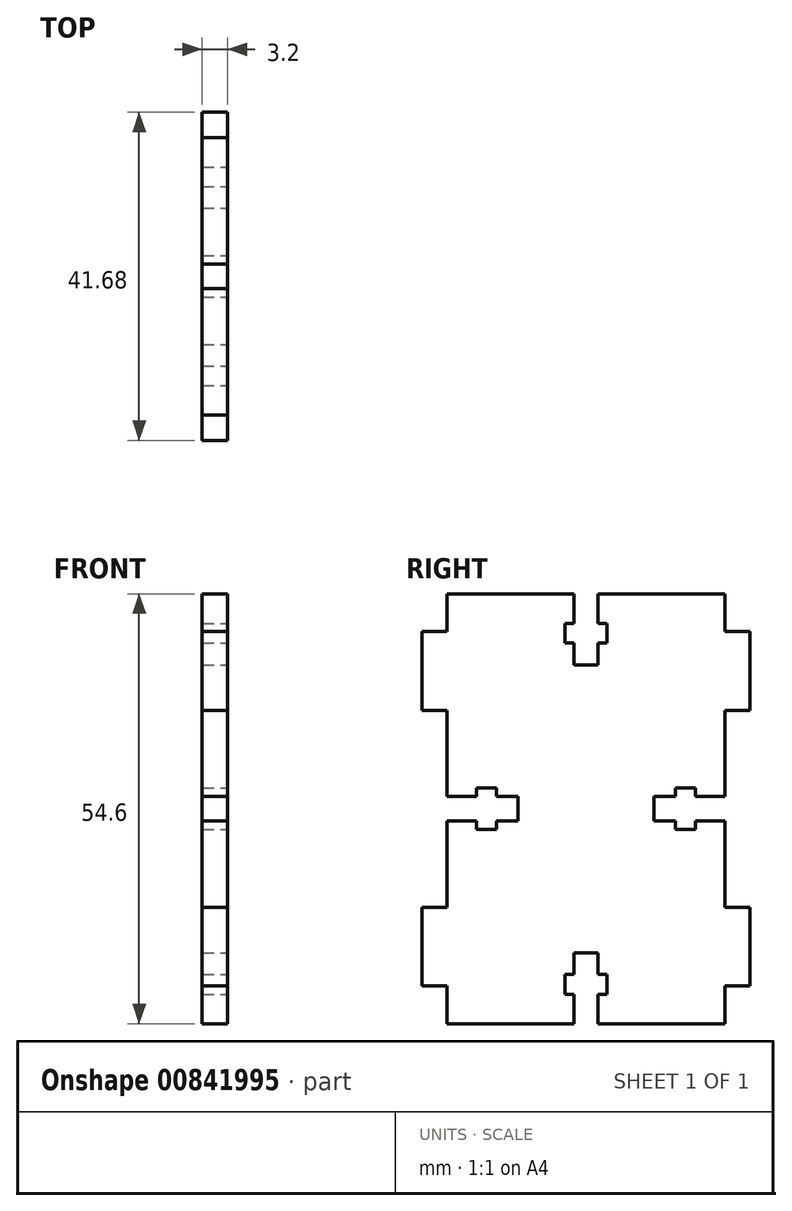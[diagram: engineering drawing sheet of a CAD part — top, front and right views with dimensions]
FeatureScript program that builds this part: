
annotation { "Feature Type Name" : "Feature", "Feature Type Description" : "" }
export const myFeature = defineFeature(function(context is Context, id is Id, definition is map)
    precondition{}
    {
        {
            assignVariable(context, id + "F0", {"name" : "mat_t", "anyValue" : 3.2});
        }
        {
            var Q0;
            Q0=qCreatedBy(makeId("Right.planeOp"),FACE);
            var sketch = newSketch(context, id + "F1", { "sketchPlane" : qUnion([Q0])});
            skLineSegment(sketch, "E0.bottom", {"start": v(-17.64, 0) * mm, "end": v(17.64, 0) * mm});
            skLineSegment(sketch, "E0.top", {"start": v(-17.64, 54.6) * mm, "end": v(17.64, 54.6) * mm});
            skLineSegment(sketch, "E0.left", {"start": v(-17.64, 0) * mm, "end": v(-17.64, 54.6) * mm});
            skLineSegment(sketch, "E0.right", {"start": v(17.64, 0) * mm, "end": v(17.64, 54.6) * mm});
            skLineSegment(sketch, "E1", {"start": v(0, 0) * mm, "end": v(0, 54.6) * mm, "construction": true});
            skSolve(sketch);
        }
        {
            var Q0;
            Q0 = qSketchRegion(id + "F1", true);
            extrude(context, id + "F2", {"entities" : qUnion([Q0]), "depth" : (getVariable(context, 'mat_t')) * mm, "offsetDistance" : 25 * mm});
        }
        {
            var Q0;
            Q0=makeQuery(id+"F2.opExtrude","CAP_FACE",FACE,{"disambiguationData":[OSD([sQuery(id+"F1.wireOp",EDGE,"E0.bottom"),sQuery(id+"F1.wireOp",EDGE,"E0.top"),sQuery(id+"F1.wireOp",EDGE,"E0.left"),sQuery(id+"F1.wireOp",EDGE,"E0.right")])],"isStart":false});
            var sketch = newSketch(context, id + "F3", { "sketchPlane" : qUnion([Q0])});
            skLineSegment(sketch, "E2", {"start": v(0, 54.6) * mm, "end": v(0, 0) * mm, "construction": true});
            skLineSegment(sketch, "E3", {"start": v(-17.64, 27.3) * mm, "end": v(17.64, 27.3) * mm, "construction": true});
            skLineSegment(sketch, "E4.bottom", {"start": v(-17.64, 49.8) * mm, "end": v(-20.84, 49.8) * mm});
            skLineSegment(sketch, "E4.top", {"start": v(-17.64, 39.8) * mm, "end": v(-20.84, 39.8) * mm});
            skLineSegment(sketch, "E4.left", {"start": v(-17.64, 49.8) * mm, "end": v(-17.64, 39.8) * mm});
            skLineSegment(sketch, "E4.right", {"start": v(-20.84, 49.8) * mm, "end": v(-20.84, 39.8) * mm});
            skLineSegment(sketch, "E5.MirrorCS", {"start": v(-20.84, 4.8) * mm, "end": v(-20.84, 14.8) * mm});
            skLineSegment(sketch, "E6.MirrorCS", {"start": v(-17.64, 4.8) * mm, "end": v(-17.64, 14.8) * mm});
            skLineSegment(sketch, "E7.MirrorCS", {"start": v(-17.64, 14.8) * mm, "end": v(-20.84, 14.8) * mm});
            skLineSegment(sketch, "E8.MirrorCS", {"start": v(-17.64, 4.8) * mm, "end": v(-20.84, 4.8) * mm});
            skLineSegment(sketch, "E9.MirrorCS", {"start": v(17.64, 4.8) * mm, "end": v(20.84, 4.8) * mm});
            skLineSegment(sketch, "E10.MirrorCS", {"start": v(17.64, 49.8) * mm, "end": v(20.84, 49.8) * mm});
            skLineSegment(sketch, "E11.MirrorCS", {"start": v(17.64, 14.8) * mm, "end": v(20.84, 14.8) * mm});
            skLineSegment(sketch, "E12.MirrorCS", {"start": v(20.84, 49.8) * mm, "end": v(20.84, 39.8) * mm});
            skLineSegment(sketch, "E13.MirrorCS", {"start": v(17.64, 39.8) * mm, "end": v(20.84, 39.8) * mm});
            skLineSegment(sketch, "E14.MirrorCS", {"start": v(20.84, 4.8) * mm, "end": v(20.84, 14.8) * mm});
            skLineSegment(sketch, "E15.MirrorCS", {"start": v(17.64, 49.8) * mm, "end": v(17.64, 39.8) * mm});
            skLineSegment(sketch, "E16.MirrorCS", {"start": v(17.64, 4.8) * mm, "end": v(17.64, 14.8) * mm});
            skLineSegment(sketch, "E17", {"start": v(-20.84, 44.8) * mm, "end": v(-17.64, 44.8) * mm, "construction": true});
            skLineSegment(sketch, "E18", {"start": v(-20.84, 9.8) * mm, "end": v(-17.64, 9.8) * mm, "construction": true});
            skSolve(sketch);
        }
        {
            var Q0;
            Q0 = qSketchRegion(id + "F3", true);
            var Q1;
            Q1=makeQuery(id+"F2.opExtrude","CAP_FACE",FACE,{"disambiguationData":[OSD([sQuery(id+"F1.wireOp",EDGE,"E0.bottom"),sQuery(id+"F1.wireOp",EDGE,"E0.top"),sQuery(id+"F1.wireOp",EDGE,"E0.left"),sQuery(id+"F1.wireOp",EDGE,"E0.right")])],"isStart":true});
            extrude(context, id + "F4", {"entities" : qUnion([Q0]), "operationType" : NewBodyOperationType.ADD, "endBound" : BoundingType.UP_TO_SURFACE, "oppositeDirection" : true, "depth" : 25 * mm, "endBoundEntityFace" : qUnion([Q1]), "offsetDistance" : 25 * mm});
        }
        {
            var Q0;
            Q0=makeQuery(id+"F4.boolean.opBoolean","MERGE",FACE,{"derivedFrom":[makeQuery(id+"F2.opExtrude","CAP_FACE",FACE,{"disambiguationData":[OSD([sQuery(id+"F1.wireOp",EDGE,"E0.bottom"),sQuery(id+"F1.wireOp",EDGE,"E0.top"),sQuery(id+"F1.wireOp",EDGE,"E0.left"),sQuery(id+"F1.wireOp",EDGE,"E0.right")])],"isStart":false}),makeQuery(id+"F4.opExtrude","CAP_FACE",FACE,{"disambiguationData":[OSD([sQuery(id+"F3.wireOp",EDGE,"E4.bottom"),sQuery(id+"F3.wireOp",EDGE,"E4.top"),sQuery(id+"F3.wireOp",EDGE,"E4.left"),sQuery(id+"F3.wireOp",EDGE,"E4.right")])],"isStart":true}),makeQuery(id+"F4.opExtrude","CAP_FACE",FACE,{"disambiguationData":[OSD([sQuery(id+"F3.wireOp",EDGE,"E5.MirrorCS"),sQuery(id+"F3.wireOp",EDGE,"E6.MirrorCS"),sQuery(id+"F3.wireOp",EDGE,"E7.MirrorCS"),sQuery(id+"F3.wireOp",EDGE,"E8.MirrorCS")])],"isStart":true}),makeQuery(id+"F4.opExtrude","CAP_FACE",FACE,{"disambiguationData":[OSD([sQuery(id+"F3.wireOp",EDGE,"E9.MirrorCS"),sQuery(id+"F3.wireOp",EDGE,"E11.MirrorCS"),sQuery(id+"F3.wireOp",EDGE,"E14.MirrorCS"),sQuery(id+"F3.wireOp",EDGE,"E16.MirrorCS")])],"isStart":true}),makeQuery(id+"F4.opExtrude","CAP_FACE",FACE,{"disambiguationData":[OSD([sQuery(id+"F3.wireOp",EDGE,"E10.MirrorCS"),sQuery(id+"F3.wireOp",EDGE,"E12.MirrorCS"),sQuery(id+"F3.wireOp",EDGE,"E13.MirrorCS"),sQuery(id+"F3.wireOp",EDGE,"E15.MirrorCS")])],"isStart":true})]});
            var sketch = newSketch(context, id + "F5", { "sketchPlane" : qUnion([Q0])});
            skLineSegment(sketch, "E19.bottom", {"start": v(1.55, 0) * mm, "end": v(1.55, 9) * mm});
            skLineSegment(sketch, "E19.top", {"start": v(-1.55, 0) * mm, "end": v(-1.55, 9) * mm});
            skLineSegment(sketch, "E19.left", {"start": v(1.55, 0) * mm, "end": v(-1.55, 0) * mm});
            skLineSegment(sketch, "E19.right", {"start": v(1.55, 9) * mm, "end": v(-1.55, 9) * mm});
            skLineSegment(sketch, "E20", {"start": v(0, 0) * mm, "end": v(0, 9) * mm, "construction": true});
            skLineSegment(sketch, "E21.bottom", {"start": v(2.65, 6.25) * mm, "end": v(2.65, 3.75) * mm});
            skLineSegment(sketch, "E21.top", {"start": v(-2.65, 6.25) * mm, "end": v(-2.65, 3.75) * mm});
            skLineSegment(sketch, "E21.left", {"start": v(2.65, 6.25) * mm, "end": v(-2.65, 6.25) * mm});
            skLineSegment(sketch, "E21.right", {"start": v(2.65, 3.75) * mm, "end": v(-2.65, 3.75) * mm});
            skPoint(sketch, "E21.middle", {"position": v(0, 5) * mm});
            skLineSegment(sketch, "E22.bottom", {"start": v(-17.64, 25.75) * mm, "end": v(-8.64, 25.75) * mm});
            skLineSegment(sketch, "E22.top", {"start": v(-17.64, 28.85) * mm, "end": v(-8.64, 28.85) * mm});
            skLineSegment(sketch, "E22.left", {"start": v(-17.64, 25.75) * mm, "end": v(-17.64, 28.85) * mm});
            skLineSegment(sketch, "E22.right", {"start": v(-8.64, 25.75) * mm, "end": v(-8.64, 28.85) * mm});
            skLineSegment(sketch, "E23", {"start": v(-17.64, 27.3) * mm, "end": v(-8.64, 27.3) * mm, "construction": true});
            skLineSegment(sketch, "E24.bottom", {"start": v(-11.39, 24.65) * mm, "end": v(-13.89, 24.65) * mm});
            skLineSegment(sketch, "E24.top", {"start": v(-11.39, 29.95) * mm, "end": v(-13.89, 29.95) * mm});
            skLineSegment(sketch, "E24.left", {"start": v(-11.39, 24.65) * mm, "end": v(-11.39, 29.95) * mm});
            skLineSegment(sketch, "E24.right", {"start": v(-13.89, 24.65) * mm, "end": v(-13.89, 29.95) * mm});
            skPoint(sketch, "E24.middle", {"position": v(-12.64, 27.3) * mm});
            skLineSegment(sketch, "E25", {"start": v(0, 54.6) * mm, "end": v(0, 0) * mm, "construction": true});
            skLineSegment(sketch, "E26.MirrorCS", {"start": v(11.39, 29.95) * mm, "end": v(13.89, 29.95) * mm});
            skLineSegment(sketch, "E27.MirrorCS", {"start": v(11.39, 24.65) * mm, "end": v(13.89, 24.65) * mm});
            skLineSegment(sketch, "E28.MirrorCS", {"start": v(17.64, 25.75) * mm, "end": v(17.64, 28.85) * mm});
            skLineSegment(sketch, "E29.MirrorCS", {"start": v(11.39, 24.65) * mm, "end": v(11.39, 29.95) * mm});
            skLineSegment(sketch, "E30.MirrorCS", {"start": v(8.64, 25.75) * mm, "end": v(8.64, 28.85) * mm});
            skLineSegment(sketch, "E31.MirrorCS", {"start": v(13.89, 24.65) * mm, "end": v(13.89, 29.95) * mm});
            skLineSegment(sketch, "E32.MirrorCS", {"start": v(17.64, 28.85) * mm, "end": v(8.64, 28.85) * mm});
            skPoint(sketch, "E33.MirrorP", {"position": v(12.64, 27.3) * mm});
            skLineSegment(sketch, "E34.MirrorCS", {"start": v(17.64, 27.3) * mm, "end": v(8.64, 27.3) * mm, "construction": true});
            skLineSegment(sketch, "E35.MirrorCS", {"start": v(17.64, 25.75) * mm, "end": v(8.64, 25.75) * mm});
            skLineSegment(sketch, "E36", {"start": v(-17.64, 27.3) * mm, "end": v(17.64, 27.3) * mm, "construction": true});
            skLineSegment(sketch, "E37.MirrorCS", {"start": v(2.65, 48.35) * mm, "end": v(2.65, 50.85) * mm});
            skLineSegment(sketch, "E38.MirrorCS", {"start": v(1.55, 54.6) * mm, "end": v(-1.55, 54.6) * mm});
            skLineSegment(sketch, "E39.MirrorCS", {"start": v(-2.65, 48.35) * mm, "end": v(-2.65, 50.85) * mm});
            skLineSegment(sketch, "E40.MirrorCS", {"start": v(2.65, 48.35) * mm, "end": v(-2.65, 48.35) * mm});
            skLineSegment(sketch, "E41.MirrorCS", {"start": v(1.55, 45.6) * mm, "end": v(-1.55, 45.6) * mm});
            skLineSegment(sketch, "E42.MirrorCS", {"start": v(2.65, 50.85) * mm, "end": v(-2.65, 50.85) * mm});
            skLineSegment(sketch, "E43.MirrorCS", {"start": v(0, 54.6) * mm, "end": v(0, 45.6) * mm, "construction": true});
            skLineSegment(sketch, "E44.MirrorCS", {"start": v(-1.55, 54.6) * mm, "end": v(-1.55, 45.6) * mm});
            skLineSegment(sketch, "E45.MirrorCS", {"start": v(1.55, 54.6) * mm, "end": v(1.55, 45.6) * mm});
            skPoint(sketch, "E46.MirrorP", {"position": v(0, 49.6) * mm});
            skSolve(sketch);
        }
        {
            var Q0;
            Q0 = qSketchRegion(id + "F5", true);
            extrude(context, id + "F6", {"entities" : qUnion([Q0]), "operationType" : NewBodyOperationType.REMOVE, "endBound" : BoundingType.THROUGH_ALL, "oppositeDirection" : true, "depth" : 25 * mm, "offsetDistance" : 25 * mm});
        }
    });
